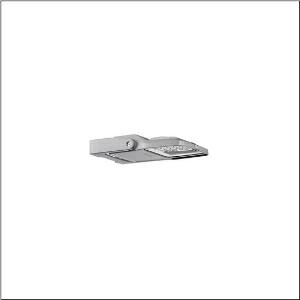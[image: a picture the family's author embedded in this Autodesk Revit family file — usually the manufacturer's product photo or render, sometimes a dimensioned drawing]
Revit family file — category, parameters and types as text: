
# Revit family: floodlight_fl_21_iq_micro___pl43_5xa7762a2a2a_df73
name_source: partatom
category: Lighting Fixtures
units: mm (PartAtom-declared; Revit-internal decimal feet)

## family parameters
Cut with Voids When Loaded = No
Host = Face
Light Source = No
Part Type = Normal
Room Calculation Point = No
Round Connector Dimension = Use Diameter
Shared = No

## types (1)
- --- (1 x LED, 3040 lm, 23.1 W, 3000K)
    Apparent Load = 23 VA
    CIE Flux Codes = 29 80 99 100 100
    Color Rendering = 70
    Color Temperature = 3000K
    Default Elevation = 1800 mm
    Description = Floodlight FL 21 iQ micro, floodlight, primary light control with lens, of PMMA, primary optical cover: protective disc, of toughened safety glass, transparent, light distribution: PL43, light emission: direct distribution, installation type: surface-mounted, LED, High Power LED, rated luminous flux: 3.040lm, luminous efficacy: 132lm/W, light colour: 730, colour temperature: 3000K, control: Auto-Match, Temp-Guard, Night-Set, Smart-Wire, Desk-Remote (wireless, voltage-free reading and setting of iQ features in the workshop via application-optimized NFC function/RFID function), optimised constant luminous flux control (CLO 2.0), Street-Remote, with terminal, 6-pole, mains connection: 220..240V, AC, 50/60Hz, start of lifetime: 23W, end of service life: 24W, reduction: 11W, luminaire housing, of diecast aluminium, powder-coated, Siteco® metallic grey (DB 702S), corrosivity category C5 mid according to DIN EN ISO 12944, sealing non-destructively replaceable, design bracket, of diecast aluminium, powder-coated, Siteco® metallic grey (DB 702S), protection rating (complete): IP66, insulation class (complete): insulation class II (safety insulation), certification: CE, ENEC, VDE, protection symbol: D, impact resistance: IK07, permissible operating ambient temperature: -40..+40°C, permissible operating ambient temperature for outdoor applications: -40..+50°C, standard: DIN EN 12944, LABS conformity tested according to VDMA 24364:2018-05, packaging unit: 1 piece

Light Distribution: PL43
    Height = 65 mm
    Lamp = 1 x LED
    Lamp Light Flux = 3040 lm
    Lamp Power = 23.1 W
    Lamp count = 1
    Length = 312 mm
    Luminous efficacy = 132 lm/W
    Manufacturer = Siteco
    ModVariant = No
    Model = 5XA7762A2A2A
    Mounting Place = Wall
    Mounting Type = Surface mounted
    Number of Poles = 1
    OnlyDefault = Yes
    Power Factor = 1
    Product Name = Floodlight FL 21 iQ micro | PL43
    Product group = floodlight | wall mounted
    ProductGroupID = 2001
    Protection Class = Protection class II
    Protection Degree = IP 66
    RLX_Detail_Level = 1
    RLX_Emergency_Light_Flux = 0 lm
    RLX_Emergency_Type = 0
    RLX_Emergency_Type_DB = No
    RlxData = <blob elided: 97321 chars, md5=c6b7d810>
    Socket = socket
    Standby Power = 0 W
    System Light Flux = 3040 lm
    System Power = 23 W
    Type Comments = factory setting: luminous flux: 100 % | dim-lin: 254 | 455 mA
    Type Image = l_1006878.jpg
    URL = http://relux.com
    VarID = @adj_127775
    Voltage = 0 V
    Weight = 0.00 kg
    Width = 230 mm

## geometry (parser evidence)
native form markers: Blend x4, Sweep x11
no freeform markers — native parametric forms only
